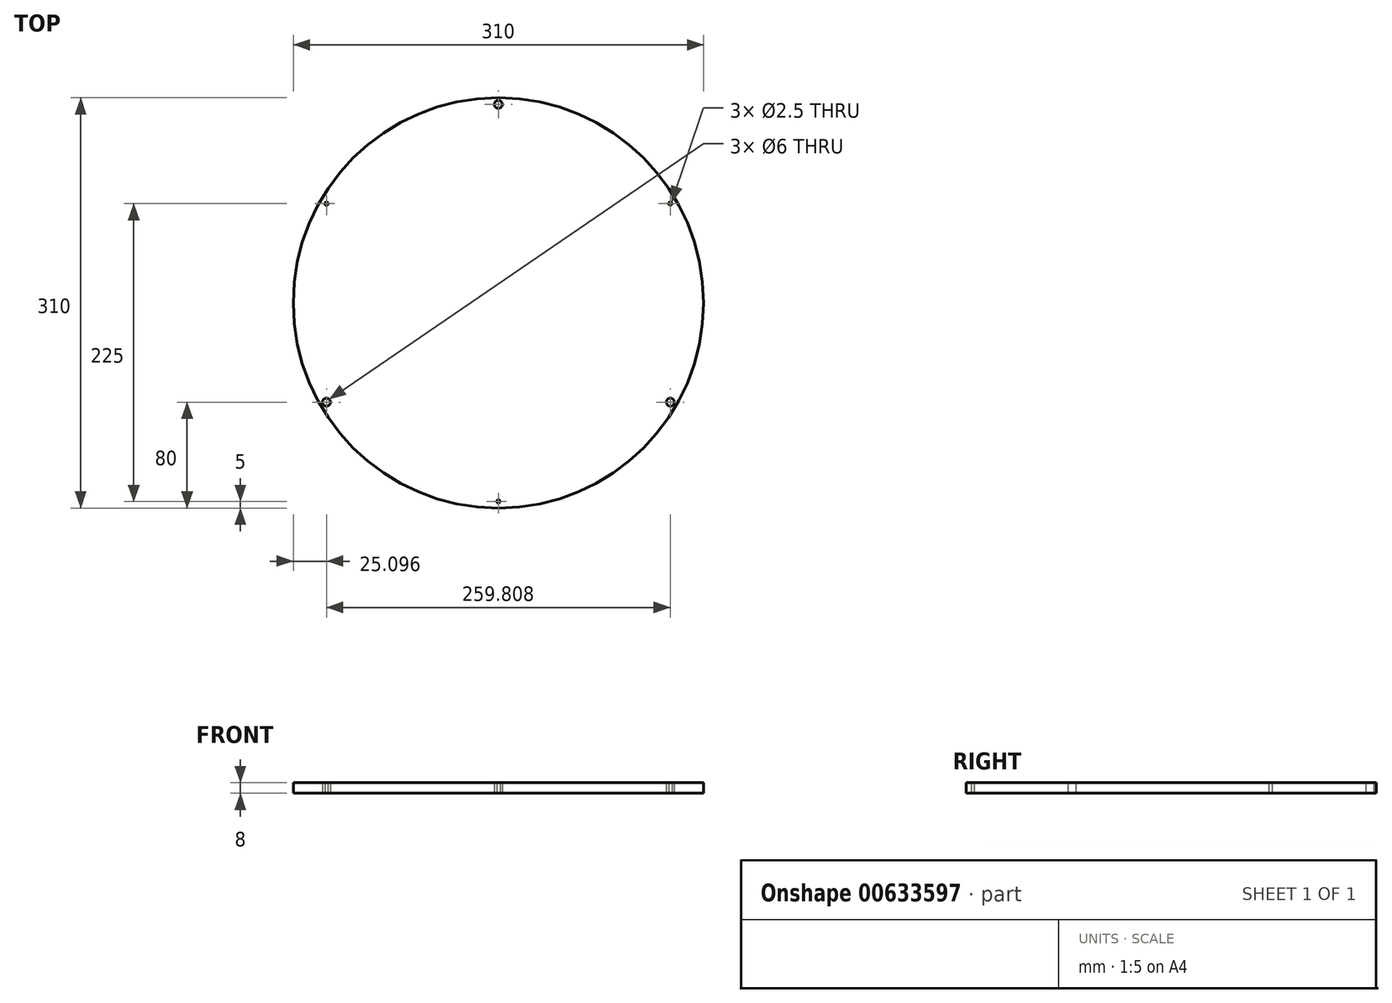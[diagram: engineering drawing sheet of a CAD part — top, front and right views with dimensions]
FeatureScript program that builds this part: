
annotation { "Feature Type Name" : "Feature", "Feature Type Description" : "" }
export const myFeature = defineFeature(function(context is Context, id is Id, definition is map)
    precondition{}
    {
        {
            var Q0;
            Q0=qCreatedBy(makeId("Top.planeOp"),FACE);
            var sketch = newSketch(context, id + "F0", { "sketchPlane" : qUnion([Q0])});
            skCircle(sketch, "E0", {"center": v(0, 0) * mm, "radius": 155 * mm});
            skCircle(sketch, "E1", {"center": v(0, 0) * mm, "radius": 150 * mm, "construction": true});
            skCircle(sketch, "E2", {"center": v(0, -150) * mm, "radius": 1.25 * mm});
            skCircle(sketch, "E3", {"center": v(0, 150) * mm, "radius": 3 * mm});
            skCircle(sketch, "E4.1.0", {"center": v(-129.9, -75) * mm, "radius": 3 * mm});
            skCircle(sketch, "E4.2.0", {"center": v(129.9, -75) * mm, "radius": 3 * mm});
            skCircle(sketch, "E5", {"center": v(0, -150) * mm, "radius": 1.5 * mm, "construction": true});
            skCircle(sketch, "E6.1.0", {"center": v(129.9, 75) * mm, "radius": 1.5 * mm, "construction": true});
            skCircle(sketch, "E6.1.1", {"center": v(129.9, 75) * mm, "radius": 1.25 * mm});
            skCircle(sketch, "E6.2.0", {"center": v(-129.9, 75) * mm, "radius": 1.5 * mm, "construction": true});
            skCircle(sketch, "E6.2.1", {"center": v(-129.9, 75) * mm, "radius": 1.25 * mm});
            skSolve(sketch);
        }
        {
            var Q0;
            Q0=qSketchRegion(id+"F0",true);
            extrude(context, id + "F1", {"entities" : qUnion([Q0]), "depth" : 8 * mm});
        }
    });
